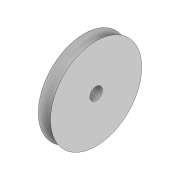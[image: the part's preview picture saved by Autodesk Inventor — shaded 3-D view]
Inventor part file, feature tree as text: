
AUTODESK INVENTOR PART (.ipt)
format: ipt  version: 2022 (Build 260153000, 153)  size: 113,664 bytes
history: native  units: mm
features: sketch x2, revolve x1, extrude x1
ambient origin geometry x8: Origin, YZ Plane, XZ Plane, XY Plane, X Axis, Y Axis, Z Axis, Center Point
bodies: Solid1 (feature_tree)
feature tree (4):
  revolve  "Revolution1"  [1 undecoded]
  extrude  "Extrusion1"  Depth=2.0mm
  sketch  "Sketch1"  dims[d0=4.0mm d1=2.0mm]
  sketch  "Sketch2"  dims[d2=15.0mm d3=2.0mm d4=90.0deg d5=4.1mm d6=10.0mm d7=0.0mm]
note: 1 required parameter value undecoded (feature->parameter linkage not recoverable at this tier; creation-order binding heuristic only, values carry confidence <= 0.55)
